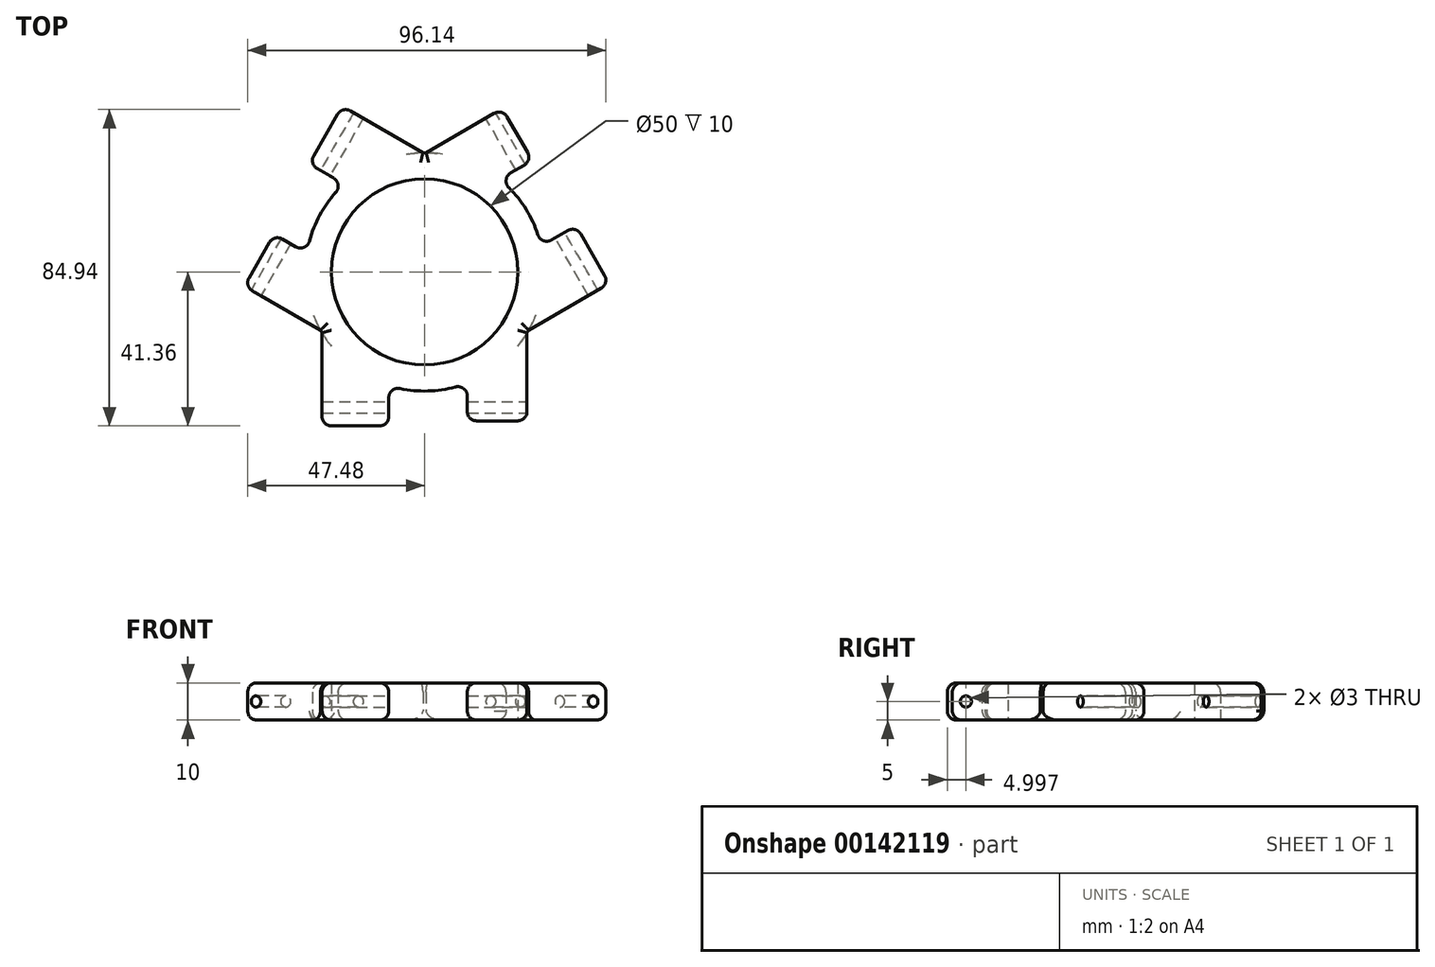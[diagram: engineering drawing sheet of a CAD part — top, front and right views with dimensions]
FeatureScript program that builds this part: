
annotation { "Feature Type Name" : "Feature", "Feature Type Description" : "" }
export const myFeature = defineFeature(function(context is Context, id is Id, definition is map)
    precondition{}
    {
        {
            var Q0;
            Q0=qCreatedBy(makeId("Top.planeOp"),FACE);
            var sketch = newSketch(context, id + "F0", { "sketchPlane" : qUnion([Q0])});
            skCircle(sketch, "E0", {"center": v(0, 0) * mm, "radius": 25 * mm});
            skCircle(sketch, "E1", {"center": v(0, 0) * mm, "radius": 32 * mm});
            skLineSegment(sketch, "E2", {"start": v(-9.6, -41.36) * mm, "end": v(-9.6, -30.53) * mm});
            skLineSegment(sketch, "E3", {"start": v(11.45, -29.88) * mm, "end": v(11.45, -40) * mm});
            skLineSegment(sketch, "E4", {"start": v(-27.5, -41.36) * mm, "end": v(-9.6, -41.36) * mm});
            skLineSegment(sketch, "E5", {"start": v(11.45, -40) * mm, "end": v(27.5, -40) * mm});
            skLineSegment(sketch, "E6", {"start": v(27.5, -40) * mm, "end": v(27.5, -16.36) * mm});
            skLineSegment(sketch, "E7", {"start": v(-27.5, -41.36) * mm, "end": v(-27.5, -16.36) * mm});
            skLineSegment(sketch, "E8.1.0", {"start": v(28.91, 29.92) * mm, "end": v(20.9, 43.82) * mm});
            skLineSegment(sketch, "E8.1.1", {"start": v(49.57, -3.13) * mm, "end": v(27.92, -15.63) * mm});
            skLineSegment(sketch, "E8.1.2", {"start": v(49.57, -3.13) * mm, "end": v(40.62, 12.37) * mm});
            skLineSegment(sketch, "E8.1.3", {"start": v(20.9, 43.82) * mm, "end": v(0.42, 32) * mm});
            skLineSegment(sketch, "E8.1.4", {"start": v(20.15, 24.86) * mm, "end": v(28.91, 29.92) * mm});
            skLineSegment(sketch, "E8.1.5", {"start": v(40.62, 12.37) * mm, "end": v(31.24, 6.95) * mm});
            skLineSegment(sketch, "E8.2.0", {"start": v(-40.37, 10.08) * mm, "end": v(-48.4, -3.82) * mm});
            skLineSegment(sketch, "E8.2.1", {"start": v(-22.07, 44.5) * mm, "end": v(-0.42, 32) * mm});
            skLineSegment(sketch, "E8.2.2", {"start": v(-22.07, 44.5) * mm, "end": v(-31.02, 29) * mm});
            skLineSegment(sketch, "E8.2.3", {"start": v(-48.4, -3.82) * mm, "end": v(-27.92, -15.63) * mm});
            skLineSegment(sketch, "E8.2.4", {"start": v(-31.6, 5.02) * mm, "end": v(-40.37, 10.08) * mm});
            skLineSegment(sketch, "E8.2.5", {"start": v(-31.02, 29) * mm, "end": v(-21.63, 23.58) * mm});
            skSolve(sketch);
        }
        {
            var Q0;
            Q0=makeQuery(id+"F0.imprint","IMPRINT",FACE,{"disambiguationData":[TD([[makeQuery(id+"F0.imprint","IMPRINT",EDGE,{"derivedFrom":sQuery(id+"F0.wireOp",EDGE,"E0")}),-1.0]])]});
            var Q1;
            Q1=makeQuery(id+"F0.imprint","IMPRINT",FACE,{"disambiguationData":[TD([[makeQuery(id+"F0.imprint","IMPRINT",EDGE,{"derivedFrom":sQuery(id+"F0.wireOp",EDGE,"E8.2.0")}),1.0]])]});
            var Q2;
            {var subQ1=sQuery(id+"F0.wireOp",EDGE,"E2");Q2=makeQuery(id+"F0.imprint","IMPRINT",FACE,{"disambiguationData":[TD([[makeQuery(id+"F0.imprint","IMPRINT",EDGE,{"derivedFrom":subQ1}),1.0]])]});}
            var Q3;
            {var subQ1=sQuery(id+"F0.wireOp",EDGE,"E8.2.1");Q3=makeQuery(id+"F0.imprint","IMPRINT",FACE,{"disambiguationData":[TD([[makeQuery(id+"F0.imprint","IMPRINT",EDGE,{"derivedFrom":subQ1}),-1.0]])]});}
            var Q4;
            Q4=makeQuery(id+"F0.imprint","IMPRINT",FACE,{"disambiguationData":[TD([[makeQuery(id+"F0.imprint","IMPRINT",EDGE,{"derivedFrom":sQuery(id+"F0.wireOp",EDGE,"E8.1.0")}),1.0]])]});
            var Q5;
            {var subQ1=sQuery(id+"F0.wireOp",EDGE,"E8.1.1");Q5=makeQuery(id+"F0.imprint","IMPRINT",FACE,{"disambiguationData":[TD([[makeQuery(id+"F0.imprint","IMPRINT",EDGE,{"derivedFrom":subQ1}),-1.0]])]});}
            var Q6;
            {var subQ0=sQuery(id+"F0.wireOp",EDGE,"E3");Q6=makeQuery(id+"F0.imprint","IMPRINT",FACE,{"disambiguationData":[TD([[makeQuery(id+"F0.imprint","IMPRINT",EDGE,{"derivedFrom":subQ0}),1.0]])]});}
            extrude(context, id + "F1", {"entities" : qUnion([Q0, Q1, Q2, Q3, Q4, Q5, Q6]), "depth" : 10 * mm});
        }
        {
            var Q0;
            Q0=makeQuery(id+"F1.opExtrude","SWEPT_FACE",FACE,{"disambiguationData":[OSD([sQuery(id+"F0.wireOp",EDGE,"E7")])]});
            var sketch = newSketch(context, id + "F2", { "sketchPlane" : qUnion([Q0])});
            skCircle(sketch, "E9", {"center": v(36.36, 5) * mm, "radius": 1.5 * mm});
            skSolve(sketch);
        }
        {
            var Q0;
            Q0=qSketchRegion(id+"F2",true);
            extrude(context, id + "F3", {"entities" : qUnion([Q0]), "depth" : 5 * mm, "hasSecondDirection" : true, "secondDirectionOppositeDirection" : true, "secondDirectionDepth" : 60 * mm});
        }
        {
            var Q0;
            Q0=makeQuery(id+"F3.opExtrude","SWEPT_BODY",BODY,{"disambiguationData":[OSD([sQuery(id+"F2.wireOp",EDGE,"E9")])]});
            var Q1;
            Q1=makeQuery(id+"F1.opExtrude","SWEPT_FACE",FACE,{"disambiguationData":[OSD([sQuery(id+"F0.wireOp",EDGE,"E0")])]});
            circularPattern(context, id + "F4", {"entities" : qUnion([Q0]), "axis" : qUnion([Q1]), "angle" : 120 * degree, "instanceCount" : 3});
        }
        {
            var Q0;
            Q0=makeQuery(id+"F3.opExtrude","SWEPT_BODY",BODY,{"disambiguationData":[OSD([sQuery(id+"F2.wireOp",EDGE,"E9")])]});
            var Q1;
            Q1=makeQuery(id+"F4.opPattern","COPY",BODY,{"derivedFrom":makeQuery(id+"F3.opExtrude","SWEPT_BODY",BODY,{"disambiguationData":[OSD([sQuery(id+"F2.wireOp",EDGE,"E9")])]}),"instanceName":"2"});
            var Q2;
            Q2=makeQuery(id+"F4.opPattern","COPY",BODY,{"derivedFrom":makeQuery(id+"F3.opExtrude","SWEPT_BODY",BODY,{"disambiguationData":[OSD([sQuery(id+"F2.wireOp",EDGE,"E9")])]}),"instanceName":"1"});
            var Q3;
            Q3=makeQuery(id+"F1.opExtrude","SWEPT_BODY",BODY,{"disambiguationData":[OSD([sQuery(id+"F0.wireOp",EDGE,"E0"),sQuery(id+"F0.wireOp",EDGE,"E1"),sQuery(id+"F0.wireOp",EDGE,"E2"),sQuery(id+"F0.wireOp",EDGE,"E3"),sQuery(id+"F0.wireOp",EDGE,"E4"),sQuery(id+"F0.wireOp",EDGE,"E5"),sQuery(id+"F0.wireOp",EDGE,"E6"),sQuery(id+"F0.wireOp",EDGE,"E7"),sQuery(id+"F0.wireOp",EDGE,"E8.1.0"),sQuery(id+"F0.wireOp",EDGE,"E8.1.1"),sQuery(id+"F0.wireOp",EDGE,"E8.1.2"),sQuery(id+"F0.wireOp",EDGE,"E8.1.3"),sQuery(id+"F0.wireOp",EDGE,"E8.1.4"),sQuery(id+"F0.wireOp",EDGE,"E8.1.5"),sQuery(id+"F0.wireOp",EDGE,"E8.2.0"),sQuery(id+"F0.wireOp",EDGE,"E8.2.1"),sQuery(id+"F0.wireOp",EDGE,"E8.2.2"),sQuery(id+"F0.wireOp",EDGE,"E8.2.3"),sQuery(id+"F0.wireOp",EDGE,"E8.2.4"),sQuery(id+"F0.wireOp",EDGE,"E8.2.5")])]});
            booleanBodies(context, id + "F5", {"operationType" : BooleanOperationType.SUBTRACTION, "tools" : qUnion([Q0, Q1, Q2]), "targets" : qUnion([Q3])});
        }
        {
            var Q0;
            Q0=makeQuery(id+"F1.opExtrude","CAP_EDGE",EDGE,{"disambiguationData":[OSD([sQuery(id+"F0.wireOp",EDGE,"E8.2.3")])],"isStart":false});
            var Q1;
            Q1=makeQuery(id+"F1.opExtrude","CAP_EDGE",EDGE,{"disambiguationData":[OSD([sQuery(id+"F0.wireOp",EDGE,"E8.2.0")])],"isStart":false});
            var Q2;
            Q2=makeQuery(id+"F1.opExtrude","SWEPT_EDGE",EDGE,{"disambiguationData":[OSD([sQuery(id+"F0.wireOp",EDGE,"E8.2.0"),sQuery(id+"F0.wireOp",EDGE,"E8.2.3")])]});
            var Q3;
            Q3=makeQuery(id+"F1.opExtrude","CAP_EDGE",EDGE,{"disambiguationData":[OSD([sQuery(id+"F0.wireOp",EDGE,"E8.2.4")])],"isStart":false});
            var Q4;
            Q4=makeQuery(id+"F1.opExtrude","SWEPT_EDGE",EDGE,{"disambiguationData":[OSD([sQuery(id+"F0.wireOp",EDGE,"E8.2.0"),sQuery(id+"F0.wireOp",EDGE,"E8.2.4")])]});
            var Q5;
            Q5=makeQuery(id+"F1.opExtrude","CAP_EDGE",EDGE,{"disambiguationData":[OSD([sQuery(id+"F0.wireOp",EDGE,"E8.2.4")])],"isStart":true});
            var Q6;
            {var subQ0=sQuery(id+"F0.wireOp",EDGE,"E1");Q6=makeQuery(id+"F1.opExtrude","CAP_EDGE",EDGE,{"disambiguationData":[OSD([subQ0]),TDD([makeQuery(id+"F0.imprint","IMPRINT",EDGE,{"disambiguationData":[TD([[makeQuery(id+"F0.imprint","INTERSECT",VERTEX,{"derivedFrom":[subQ0,sQuery(id+"F0.wireOp",EDGE,"E8.2.4")]}),1.0]])],"derivedFrom":subQ0})])],"isStart":false});}
            var Q7;
            Q7=makeQuery(id+"F1.opExtrude","CAP_EDGE",EDGE,{"disambiguationData":[OSD([sQuery(id+"F0.wireOp",EDGE,"E8.2.5")])],"isStart":false});
            var Q8;
            Q8=makeQuery(id+"F1.opExtrude","CAP_EDGE",EDGE,{"disambiguationData":[OSD([sQuery(id+"F0.wireOp",EDGE,"E8.2.2")])],"isStart":false});
            var Q9;
            Q9=makeQuery(id+"F1.opExtrude","SWEPT_EDGE",EDGE,{"disambiguationData":[OSD([sQuery(id+"F0.wireOp",EDGE,"E8.2.2"),sQuery(id+"F0.wireOp",EDGE,"E8.2.5")])]});
            var Q10;
            Q10=makeQuery(id+"F1.opExtrude","SWEPT_EDGE",EDGE,{"disambiguationData":[OSD([sQuery(id+"F0.wireOp",EDGE,"E8.2.1"),sQuery(id+"F0.wireOp",EDGE,"E8.2.2")])]});
            var Q11;
            Q11=makeQuery(id+"F1.opExtrude","CAP_EDGE",EDGE,{"disambiguationData":[OSD([sQuery(id+"F0.wireOp",EDGE,"E8.2.1")])],"isStart":false});
            var Q12;
            Q12=makeQuery(id+"F1.opExtrude","CAP_EDGE",EDGE,{"disambiguationData":[OSD([sQuery(id+"F0.wireOp",EDGE,"E8.1.3")])],"isStart":false});
            var Q13;
            {var subQ0=sQuery(id+"F0.wireOp",EDGE,"E1");Q13=makeQuery(id+"F1.opExtrude","CAP_EDGE",EDGE,{"disambiguationData":[OSD([subQ0]),TDD([makeQuery(id+"F0.imprint","IMPRINT",EDGE,{"disambiguationData":[TD([[makeQuery(id+"F0.imprint","INTERSECT",VERTEX,{"derivedFrom":[subQ0,sQuery(id+"F0.wireOp",EDGE,"E8.1.4")]}),1.0]])],"derivedFrom":subQ0})])],"isStart":false});}
            var Q14;
            Q14=makeQuery(id+"F1.opExtrude","CAP_EDGE",EDGE,{"disambiguationData":[OSD([sQuery(id+"F0.wireOp",EDGE,"E8.1.0")])],"isStart":false});
            var Q15;
            Q15=makeQuery(id+"F1.opExtrude","CAP_EDGE",EDGE,{"disambiguationData":[OSD([sQuery(id+"F0.wireOp",EDGE,"E8.1.0")])],"isStart":true});
            var Q16;
            Q16=makeQuery(id+"F1.opExtrude","SWEPT_EDGE",EDGE,{"disambiguationData":[OSD([sQuery(id+"F0.wireOp",EDGE,"E8.1.0"),sQuery(id+"F0.wireOp",EDGE,"E8.1.3")])]});
            var Q17;
            Q17=makeQuery(id+"F1.opExtrude","CAP_EDGE",EDGE,{"disambiguationData":[OSD([sQuery(id+"F0.wireOp",EDGE,"E8.2.1")])],"isStart":true});
            var Q18;
            {var subQ0=sQuery(id+"F0.wireOp",EDGE,"E1");Q18=makeQuery(id+"F1.opExtrude","CAP_EDGE",EDGE,{"disambiguationData":[OSD([subQ0]),TDD([makeQuery(id+"F0.imprint","IMPRINT",EDGE,{"disambiguationData":[TD([[makeQuery(id+"F0.imprint","INTERSECT",VERTEX,{"derivedFrom":[subQ0,sQuery(id+"F0.wireOp",EDGE,"E8.1.4")]}),1.0]])],"derivedFrom":subQ0})])],"isStart":true});}
            var Q19;
            Q19=makeQuery(id+"F1.opExtrude","SWEPT_EDGE",EDGE,{"disambiguationData":[OSD([sQuery(id+"F0.wireOp",EDGE,"E8.1.0"),sQuery(id+"F0.wireOp",EDGE,"E8.1.4")])]});
            var Q20;
            Q20=makeQuery(id+"F1.opExtrude","CAP_EDGE",EDGE,{"disambiguationData":[OSD([sQuery(id+"F0.wireOp",EDGE,"E8.1.4")])],"isStart":false});
            var Q21;
            Q21=makeQuery(id+"F1.opExtrude","CAP_EDGE",EDGE,{"disambiguationData":[OSD([sQuery(id+"F0.wireOp",EDGE,"E8.1.5")])],"isStart":false});
            var Q22;
            Q22=makeQuery(id+"F1.opExtrude","CAP_EDGE",EDGE,{"disambiguationData":[OSD([sQuery(id+"F0.wireOp",EDGE,"E8.1.2")])],"isStart":false});
            var Q23;
            Q23=makeQuery(id+"F1.opExtrude","CAP_EDGE",EDGE,{"disambiguationData":[OSD([sQuery(id+"F0.wireOp",EDGE,"E8.1.2")])],"isStart":true});
            var Q24;
            Q24=makeQuery(id+"F1.opExtrude","SWEPT_EDGE",EDGE,{"disambiguationData":[OSD([sQuery(id+"F0.wireOp",EDGE,"E8.1.1"),sQuery(id+"F0.wireOp",EDGE,"E8.1.2")])]});
            var Q25;
            Q25=makeQuery(id+"F1.opExtrude","SWEPT_EDGE",EDGE,{"disambiguationData":[OSD([sQuery(id+"F0.wireOp",EDGE,"E8.1.2"),sQuery(id+"F0.wireOp",EDGE,"E8.1.5")])]});
            var Q26;
            Q26=makeQuery(id+"F1.opExtrude","CAP_EDGE",EDGE,{"disambiguationData":[OSD([sQuery(id+"F0.wireOp",EDGE,"E8.1.1")])],"isStart":false});
            var Q27;
            Q27=makeQuery(id+"F1.opExtrude","CAP_EDGE",EDGE,{"disambiguationData":[OSD([sQuery(id+"F0.wireOp",EDGE,"E8.1.1")])],"isStart":true});
            var Q28;
            Q28=makeQuery(id+"F1.opExtrude","CAP_EDGE",EDGE,{"disambiguationData":[OSD([sQuery(id+"F0.wireOp",EDGE,"E6")])],"isStart":false});
            var Q29;
            Q29=makeQuery(id+"F1.opExtrude","CAP_EDGE",EDGE,{"disambiguationData":[OSD([sQuery(id+"F0.wireOp",EDGE,"E6")])],"isStart":true});
            var Q30;
            Q30=makeQuery(id+"F1.opExtrude","SWEPT_EDGE",EDGE,{"disambiguationData":[OSD([sQuery(id+"F0.wireOp",EDGE,"E5"),sQuery(id+"F0.wireOp",EDGE,"E6")])]});
            var Q31;
            Q31=makeQuery(id+"F1.opExtrude","CAP_EDGE",EDGE,{"disambiguationData":[OSD([sQuery(id+"F0.wireOp",EDGE,"E5")])],"isStart":false});
            var Q32;
            Q32=makeQuery(id+"F1.opExtrude","CAP_EDGE",EDGE,{"disambiguationData":[OSD([sQuery(id+"F0.wireOp",EDGE,"E3")])],"isStart":false});
            var Q33;
            Q33=makeQuery(id+"F1.opExtrude","CAP_EDGE",EDGE,{"disambiguationData":[OSD([sQuery(id+"F0.wireOp",EDGE,"E5")])],"isStart":true});
            var Q34;
            Q34=makeQuery(id+"F1.opExtrude","SWEPT_EDGE",EDGE,{"disambiguationData":[OSD([sQuery(id+"F0.wireOp",EDGE,"E3"),sQuery(id+"F0.wireOp",EDGE,"E5")])]});
            var Q35;
            {var subQ0=sQuery(id+"F0.wireOp",EDGE,"E1");Q35=makeQuery(id+"F1.opExtrude","CAP_EDGE",EDGE,{"disambiguationData":[OSD([subQ0]),TDD([makeQuery(id+"F0.imprint","IMPRINT",EDGE,{"disambiguationData":[TD([[makeQuery(id+"F0.imprint","INTERSECT",VERTEX,{"derivedFrom":[subQ0,sQuery(id+"F0.wireOp",EDGE,"E2")]}),-1.0]])],"derivedFrom":subQ0})])],"isStart":false});}
            var Q36;
            {var subQ0=sQuery(id+"F0.wireOp",EDGE,"E1");Q36=makeQuery(id+"F1.opExtrude","CAP_EDGE",EDGE,{"disambiguationData":[OSD([subQ0]),TDD([makeQuery(id+"F0.imprint","IMPRINT",EDGE,{"disambiguationData":[TD([[makeQuery(id+"F0.imprint","INTERSECT",VERTEX,{"derivedFrom":[subQ0,sQuery(id+"F0.wireOp",EDGE,"E2")]}),-1.0]])],"derivedFrom":subQ0})])],"isStart":true});}
            var Q37;
            Q37=makeQuery(id+"F1.opExtrude","CAP_EDGE",EDGE,{"disambiguationData":[OSD([sQuery(id+"F0.wireOp",EDGE,"E2")])],"isStart":false});
            var Q38;
            Q38=makeQuery(id+"F1.opExtrude","CAP_EDGE",EDGE,{"disambiguationData":[OSD([sQuery(id+"F0.wireOp",EDGE,"E2")])],"isStart":true});
            var Q39;
            Q39=makeQuery(id+"F1.opExtrude","CAP_EDGE",EDGE,{"disambiguationData":[OSD([sQuery(id+"F0.wireOp",EDGE,"E4")])],"isStart":true});
            var Q40;
            Q40=makeQuery(id+"F1.opExtrude","CAP_EDGE",EDGE,{"disambiguationData":[OSD([sQuery(id+"F0.wireOp",EDGE,"E4")])],"isStart":false});
            var Q41;
            Q41=makeQuery(id+"F1.opExtrude","CAP_EDGE",EDGE,{"disambiguationData":[OSD([sQuery(id+"F0.wireOp",EDGE,"E7")])],"isStart":false});
            var Q42;
            Q42=makeQuery(id+"F1.opExtrude","CAP_EDGE",EDGE,{"disambiguationData":[OSD([sQuery(id+"F0.wireOp",EDGE,"E7")])],"isStart":true});
            var Q43;
            Q43=makeQuery(id+"F1.opExtrude","CAP_EDGE",EDGE,{"disambiguationData":[OSD([sQuery(id+"F0.wireOp",EDGE,"E8.2.3")])],"isStart":true});
            var Q44;
            Q44=makeQuery(id+"F1.opExtrude","CAP_EDGE",EDGE,{"disambiguationData":[OSD([sQuery(id+"F0.wireOp",EDGE,"E8.2.2")])],"isStart":true});
            var Q45;
            Q45=makeQuery(id+"F1.opExtrude","CAP_EDGE",EDGE,{"disambiguationData":[OSD([sQuery(id+"F0.wireOp",EDGE,"E8.2.5")])],"isStart":true});
            var Q46;
            Q46=makeQuery(id+"F1.opExtrude","CAP_EDGE",EDGE,{"disambiguationData":[OSD([sQuery(id+"F0.wireOp",EDGE,"E8.1.3")])],"isStart":true});
            var Q47;
            Q47=makeQuery(id+"F1.opExtrude","CAP_EDGE",EDGE,{"disambiguationData":[OSD([sQuery(id+"F0.wireOp",EDGE,"E3")])],"isStart":true});
            var Q48;
            Q48=makeQuery(id+"F1.opExtrude","CAP_EDGE",EDGE,{"disambiguationData":[OSD([sQuery(id+"F0.wireOp",EDGE,"E8.1.5")])],"isStart":true});
            var Q49;
            Q49=makeQuery(id+"F1.opExtrude","CAP_EDGE",EDGE,{"disambiguationData":[OSD([sQuery(id+"F0.wireOp",EDGE,"E8.1.4")])],"isStart":true});
            var Q50;
            {var subQ0=sQuery(id+"F0.wireOp",EDGE,"E1");Q50=makeQuery(id+"F1.opExtrude","CAP_EDGE",EDGE,{"disambiguationData":[OSD([subQ0]),TDD([makeQuery(id+"F0.imprint","IMPRINT",EDGE,{"disambiguationData":[TD([[makeQuery(id+"F0.imprint","INTERSECT",VERTEX,{"derivedFrom":[subQ0,sQuery(id+"F0.wireOp",EDGE,"E8.1.3")]}),-1.0]])],"derivedFrom":subQ0})])],"isStart":false});}
            var Q51;
            {var subQ0=sQuery(id+"F0.wireOp",EDGE,"E1");Q51=makeQuery(id+"F1.opExtrude","CAP_EDGE",EDGE,{"disambiguationData":[OSD([subQ0]),TDD([makeQuery(id+"F0.imprint","IMPRINT",EDGE,{"disambiguationData":[TD([[makeQuery(id+"F0.imprint","INTERSECT",VERTEX,{"derivedFrom":[subQ0,sQuery(id+"F0.wireOp",EDGE,"E7")]}),1.0]])],"derivedFrom":subQ0})])],"isStart":false});}
            var Q52;
            {var subQ0=sQuery(id+"F0.wireOp",EDGE,"E1");Q52=makeQuery(id+"F1.opExtrude","CAP_EDGE",EDGE,{"disambiguationData":[OSD([subQ0]),TDD([makeQuery(id+"F0.imprint","IMPRINT",EDGE,{"disambiguationData":[TD([[makeQuery(id+"F0.imprint","INTERSECT",VERTEX,{"derivedFrom":[subQ0,sQuery(id+"F0.wireOp",EDGE,"E6")]}),-1.0]])],"derivedFrom":subQ0})])],"isStart":false});}
            var Q53;
            Q53=makeQuery(id+"F1.opExtrude","CAP_EDGE",EDGE,{"disambiguationData":[OSD([sQuery(id+"F0.wireOp",EDGE,"E8.2.0")])],"isStart":true});
            var Q54;
            Q54=makeQuery(id+"F1.opExtrude","SWEPT_EDGE",EDGE,{"disambiguationData":[OSD([sQuery(id+"F0.wireOp",EDGE,"E4"),sQuery(id+"F0.wireOp",EDGE,"E7")])]});
            var Q55;
            Q55=makeQuery(id+"F1.opExtrude","SWEPT_EDGE",EDGE,{"disambiguationData":[OSD([sQuery(id+"F0.wireOp",EDGE,"E2"),sQuery(id+"F0.wireOp",EDGE,"E4")])]});
            var Q56;
            Q56=makeQuery(id+"F1.opExtrude","SWEPT_EDGE",EDGE,{"disambiguationData":[OSD([sQuery(id+"F0.wireOp",EDGE,"E1"),sQuery(id+"F0.wireOp",EDGE,"E8.1.5")])]});
            var Q57;
            Q57=makeQuery(id+"F1.opExtrude","SWEPT_EDGE",EDGE,{"disambiguationData":[OSD([sQuery(id+"F0.wireOp",EDGE,"E1"),sQuery(id+"F0.wireOp",EDGE,"E8.1.4")])]});
            var Q58;
            Q58=makeQuery(id+"F1.opExtrude","SWEPT_EDGE",EDGE,{"disambiguationData":[OSD([sQuery(id+"F0.wireOp",EDGE,"E1"),sQuery(id+"F0.wireOp",EDGE,"E8.2.5")])]});
            var Q59;
            Q59=makeQuery(id+"F1.opExtrude","SWEPT_EDGE",EDGE,{"disambiguationData":[OSD([sQuery(id+"F0.wireOp",EDGE,"E1"),sQuery(id+"F0.wireOp",EDGE,"E8.2.4")])]});
            var Q60;
            Q60=makeQuery(id+"F1.opExtrude","SWEPT_EDGE",EDGE,{"disambiguationData":[OSD([sQuery(id+"F0.wireOp",EDGE,"E1"),sQuery(id+"F0.wireOp",EDGE,"E2")])]});
            var Q61;
            Q61=makeQuery(id+"F1.opExtrude","SWEPT_EDGE",EDGE,{"disambiguationData":[OSD([sQuery(id+"F0.wireOp",EDGE,"E1"),sQuery(id+"F0.wireOp",EDGE,"E3")])]});
            fillet(context, id + "F6", {"entities" : qUnion([Q0, Q1, Q2, Q3, Q4, Q5, Q6, Q7, Q8, Q9, Q10, Q11, Q12, Q13, Q14, Q15, Q16, Q17, Q18, Q19, Q20, Q21, Q22, Q23, Q24, Q25, Q26, Q27, Q28, Q29, Q30, Q31, Q32, Q33, Q34, Q35, Q36, Q37, Q38, Q39, Q40, Q41, Q42, Q43, Q44, Q45, Q46, Q47, Q48, Q49, Q50, Q51, Q52, Q53, Q54, Q55, Q56, Q57, Q58, Q59, Q60, Q61]), "radius" : 2.5 * mm, "tangentPropagation" : true, "allowEdgeOverflow" : false});
        }
    });
